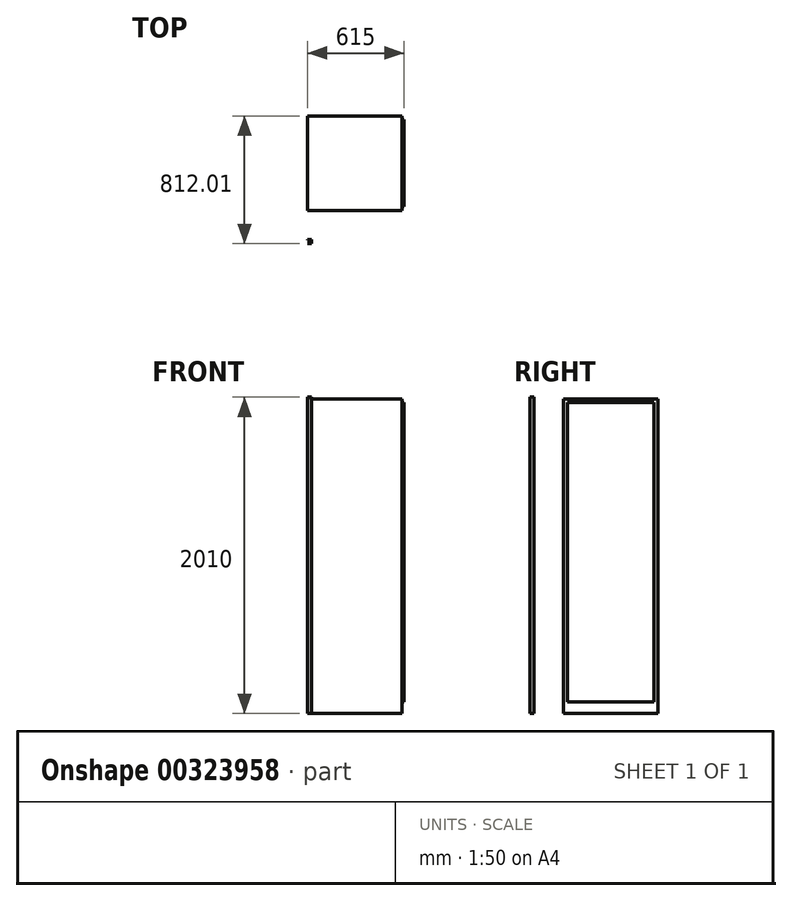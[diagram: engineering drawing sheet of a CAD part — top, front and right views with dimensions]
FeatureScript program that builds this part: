
annotation { "Feature Type Name" : "Feature", "Feature Type Description" : "" }
export const myFeature = defineFeature(function(context is Context, id is Id, definition is map)
    precondition{}
    {
        {
            var Q0;
            Q0=qCreatedBy(makeId("Right.planeOp"),FACE);
            var sketch = newSketch(context, id + "F0", { "sketchPlane" : qUnion([Q0])});
            skLineSegment(sketch, "E0.bottom", {"start": v(0, 0) * mm, "end": v(600, 0) * mm});
            skLineSegment(sketch, "E0.top", {"start": v(0, 2000) * mm, "end": v(600, 2000) * mm});
            skLineSegment(sketch, "E0.left", {"start": v(0, 0) * mm, "end": v(0, 2000) * mm});
            skLineSegment(sketch, "E0.right", {"start": v(600, 0) * mm, "end": v(600, 2000) * mm});
            skSolve(sketch);
        }
        {
            var Q0;
            Q0 = qSketchRegion(id + "F0", true);
            extrude(context, id + "F1", {"entities" : qUnion([Q0]), "depth" : 600 * mm, "offsetDistance" : 25 * mm});
        }
        {
            var Q0;
            Q0=makeQuery(id+"F1.opExtrude","CAP_FACE",FACE,{"disambiguationData":[OSD([sQuery(id+"F0.wireOp",EDGE,"E0.bottom"),sQuery(id+"F0.wireOp",EDGE,"E0.top"),sQuery(id+"F0.wireOp",EDGE,"E0.left"),sQuery(id+"F0.wireOp",EDGE,"E0.right")])],"isStart":false});
            var sketch = newSketch(context, id + "F2", { "sketchPlane" : qUnion([Q0])});
            skLineSegment(sketch, "E1.bottom", {"start": v(25, 1975) * mm, "end": v(575, 1975) * mm});
            skLineSegment(sketch, "E1.top", {"start": v(25, 75) * mm, "end": v(575, 75) * mm});
            skLineSegment(sketch, "E1.left", {"start": v(25, 1975) * mm, "end": v(25, 75) * mm});
            skLineSegment(sketch, "E1.right", {"start": v(575, 1975) * mm, "end": v(575, 75) * mm});
            skLineSegment(sketch, "E2", {"start": v(300, 2000) * mm, "end": v(300, 0) * mm, "construction": true});
            skSolve(sketch);
        }
        {
            var Q0;
            Q0 = qSketchRegion(id + "F2", true);
            extrude(context, id + "F3", {"entities" : qUnion([Q0]), "operationType" : NewBodyOperationType.ADD, "depth" : 15 * mm, "offsetDistance" : 25 * mm});
        }
        {
            var Q0;
            Q0=qCreatedBy(makeId("Right.planeOp"),FACE);
            var sketch = newSketch(context, id + "F4", { "sketchPlane" : qUnion([Q0])});
            skLineSegment(sketch, "E3.bottom", {"start": v(-187.01, 0) * mm, "end": v(-212.01, 0) * mm});
            skLineSegment(sketch, "E3.top", {"start": v(-187.01, 2010) * mm, "end": v(-212.01, 2010) * mm});
            skLineSegment(sketch, "E3.left", {"start": v(-187.01, 0) * mm, "end": v(-187.01, 2010) * mm});
            skLineSegment(sketch, "E3.right", {"start": v(-212.01, 0) * mm, "end": v(-212.01, 2010) * mm});
            skSolve(sketch);
        }
        {
            var Q0;
            Q0 = qSketchRegion(id + "F4", true);
            extrude(context, id + "F5", {"entities" : qUnion([Q0]), "depth" : 25 * mm, "offsetDistance" : 25 * mm});
        }
        {
            var Q0;
            Q0=makeQuery(id+"F5.opExtrude","CAP_FACE",FACE,{"disambiguationData":[OSD([sQuery(id+"F4.wireOp",EDGE,"E3.bottom"),sQuery(id+"F4.wireOp",EDGE,"E3.top"),sQuery(id+"F4.wireOp",EDGE,"E3.left"),sQuery(id+"F4.wireOp",EDGE,"E3.right")])],"isStart":true});
            var sketch = newSketch(context, id + "F6", { "sketchPlane" : qUnion([Q0])});
            skLineSegment(sketch, "E4.bottom", {"start": v(189.01, 2010) * mm, "end": v(210.01, 2010) * mm});
            skLineSegment(sketch, "E4.top", {"start": v(189.01, 0) * mm, "end": v(210.01, 0) * mm});
            skLineSegment(sketch, "E4.left", {"start": v(189.01, 2010) * mm, "end": v(189.01, 0) * mm});
            skLineSegment(sketch, "E4.right", {"start": v(210.01, 2010) * mm, "end": v(210.01, 0) * mm});
            skLineSegment(sketch, "E5", {"start": v(199.51, 0) * mm, "end": v(199.51, 2010) * mm, "construction": true});
            skSolve(sketch);
        }
        {
            var Q0;
            Q0 = qSketchRegion(id + "F6", true);
            var Q1;
            Q1=makeQuery(id+"F5.opExtrude","CAP_FACE",FACE,{"disambiguationData":[OSD([sQuery(id+"F4.wireOp",EDGE,"E3.bottom"),sQuery(id+"F4.wireOp",EDGE,"E3.top"),sQuery(id+"F4.wireOp",EDGE,"E3.left"),sQuery(id+"F4.wireOp",EDGE,"E3.right")])],"isStart":false});
            extrude(context, id + "F7", {"entities" : qUnion([Q0]), "operationType" : NewBodyOperationType.REMOVE, "endBound" : BoundingType.UP_TO_SURFACE, "oppositeDirection" : true, "depth" : 25 * mm, "endBoundEntityFace" : qUnion([Q1]), "hasOffset" : true, "offsetDistance" : 2 * mm});
        }
    });
